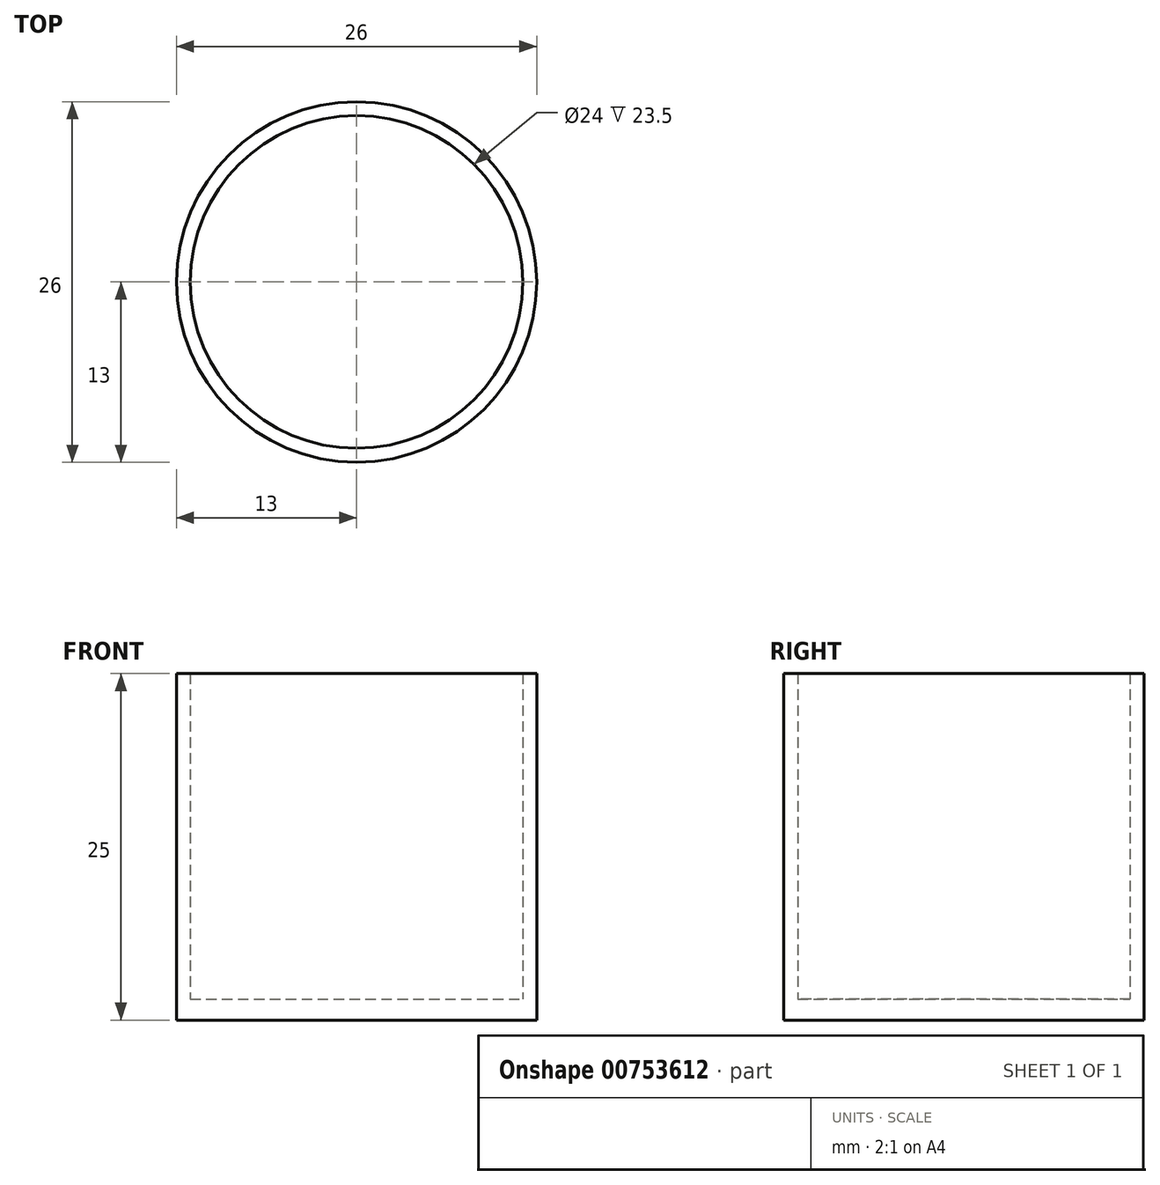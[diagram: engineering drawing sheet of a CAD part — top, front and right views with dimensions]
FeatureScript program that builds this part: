
annotation { "Feature Type Name" : "Feature", "Feature Type Description" : "" }
export const myFeature = defineFeature(function(context is Context, id is Id, definition is map)
    precondition{}
    {
        {
            var Q0;
            Q0=qCreatedBy(makeId("Right.planeOp"),FACE);
            var sketch = newSketch(context, id + "F0", { "sketchPlane" : qUnion([Q0])});
            skLineSegment(sketch, "E0", {"start": v(-13, 25) * mm, "end": v(-12, 25) * mm});
            skLineSegment(sketch, "E1", {"start": v(-12, 1.5) * mm, "end": v(-12, 25) * mm});
            skLineSegment(sketch, "E2", {"start": v(-12, 1.5) * mm, "end": v(0, 1.5) * mm});
            skLineSegment(sketch, "E3", {"start": v(-13, 25) * mm, "end": v(-13, 0) * mm});
            skLineSegment(sketch, "E4", {"start": v(-13, 0) * mm, "end": v(0, 0) * mm});
            skLineSegment(sketch, "E5", {"start": v(0, 0) * mm, "end": v(0, 1.5) * mm});
            skSolve(sketch);
        }
        {
            var Q0;
            Q0=makeQuery(id+"F0.imprint","IMPRINT",FACE,{"disambiguationData":[TD([[makeQuery(id+"F0.imprint","IMPRINT",EDGE,{"derivedFrom":sQuery(id+"F0.wireOp",EDGE,"E0")}),-1.0]])]});
            var Q1;
            Q1=sQuery(id+"F0.wireOp",EDGE,"E5");
            revolve(context, id + "F1", {"surfaceOperationType" : NewSurfaceOperationType.NEW, "entities" : qUnion([Q0]), "axis" : qUnion([Q1]), "revolveType" : RevolveType.FULL});
        }
    });
